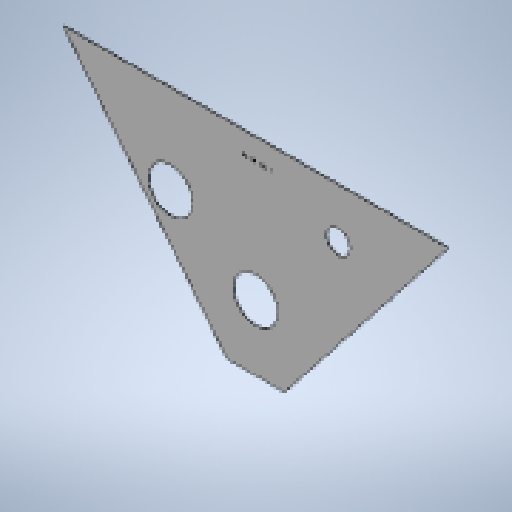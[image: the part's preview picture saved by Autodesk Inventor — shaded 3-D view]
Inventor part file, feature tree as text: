
AUTODESK INVENTOR PART (.ipt)
format: ipt  version: 2025 (Build 290162010, 162A)  size: 274,944 bytes
history: native  units: mm
features: other x3, sketch x3, sheet_metal_op x1, mirror x1, extrude x1, projected_geometry x1
ambient origin geometry x8: Origin, YZ Plane, XZ Plane, XY Plane, X Axis, Y Axis, Z Axis, Center Point
bodies: Solid1 (feature_tree)
feature tree (10):
  sheet_metal_op  "Face1"
  mirror  "Mirror1"
  extrude  "Extrusion1"  Depth=2.0mm
  other  "Mark1"
  sketch  "Sketch1"  dims[d1=735.090647mm d2=2.0mm]
  other  "Plate1"
  sketch  "Sketch2"  dims[d3=2.0mm]
  projected_geometry  "Projected Loop1"
  sketch  "Sketch3"  dims[d5=22.414154mm d6=110.0mm d9=790.0mm d13=169.0mm d14=0.0mm d15=0.0mm d16=250.0mm d17=450.0mm d18=325.0mm d19=31.0mm d20=90.0mm d21=156.0mm d23=315.0mm d24=600.0mm d25=12.0mm d26=110.0mm d28=22.414154mm]
  other  "Definition1"
